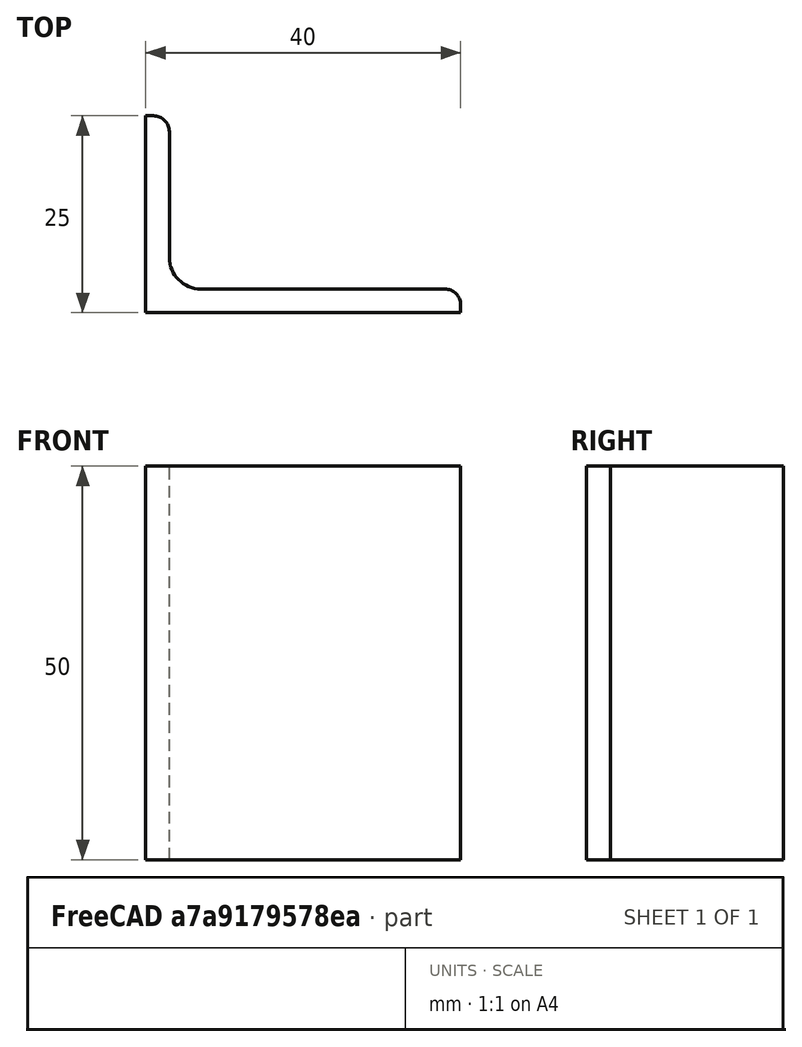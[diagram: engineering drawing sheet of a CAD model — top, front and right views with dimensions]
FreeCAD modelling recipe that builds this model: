
FCSTD DOCUMENT  (FreeCAD 0.15R4671 (Git))
Label: Angle Bar 40x25x3 EN10056 S235JR
License: All rights reserved
LicenseURL: http://en.wikipedia.org/wiki/All_rights_reserved
objects: Sketcher::SketchObject×1, Part::Extrusion×1
note: 2 computed .brp shape members not serialized (recipe doc carries the construction recipe); baked Part::Feature solids carry a one-line shape summary decoded from their .brp

FEATURE [Sketcher::SketchObject] Sketch
  sketch-geometry (9):
    g0: LineSegment StartX=0 StartY=0 StartZ=0 EndX=40 EndY=0 EndZ=0
    g1: LineSegment StartX=40 StartY=0 StartZ=0 EndX=40 EndY=1 EndZ=0
    g2: LineSegment StartX=38 StartY=3 StartZ=0 EndX=7 EndY=3 EndZ=0
    g3: LineSegment StartX=0 StartY=0 StartZ=0 EndX=0 EndY=25 EndZ=0
    g4: LineSegment StartX=0 StartY=25 StartZ=0 EndX=1 EndY=25 EndZ=0
    g5: LineSegment StartX=3 StartY=23 StartZ=0 EndX=3 EndY=7 EndZ=0
    g6: ArcOfCircle CenterX=7 CenterY=7 CenterZ=0 NormalX=0 NormalY=0 NormalZ=1 Radius=4 StartAngle=3.14159 EndAngle=4.71239
    g7: ArcOfCircle CenterX=1 CenterY=23 CenterZ=0 NormalX=0 NormalY=0 NormalZ=1 Radius=2 StartAngle=0 EndAngle=1.5708
    g8: ArcOfCircle CenterX=38 CenterY=1 CenterZ=0 NormalX=0 NormalY=0 NormalZ=1 Radius=2 StartAngle=0 EndAngle=1.5708
  constraints (23):
    c: Coincident(g0,g-1)
    c: Horizontal(g0)
    c: Coincident(g1,g0)
    c: Vertical(g1)
    c: Horizontal(g2)
    c: Coincident(g3,g-1)
    c: Vertical(g3)
    c: Coincident(g4,g3)
    c: Horizontal(g4)
    c: Vertical(g5)
    c: Tangent(g5,g6) = -1.5708
    c: Tangent(g2,g6) = 1.5708
    c: Tangent(g4,g7) = 1.5708
    c: Tangent(g5,g7) = 1.5708
    c: Tangent(g2,g8) = -1.5708
    c: Tangent(g1,g8) = -1.5708
    c: DistanceX(g0) = 40
    c: DistanceY(g3) = 25
    c: DistanceY(g0,g2) = 3
    c: DistanceX(g3,g5) = 3
    c: Radius(g6) = 4
    c: Radius(g8) = 2
    c: Radius(g7) = 2
FEATURE [Part::Extrusion] Extrude  label="Angle Bar 40x25x3 EN10056 S235JR"
  Base = -> Sketch
  Dir = (0,0,50)
  Solid = true
